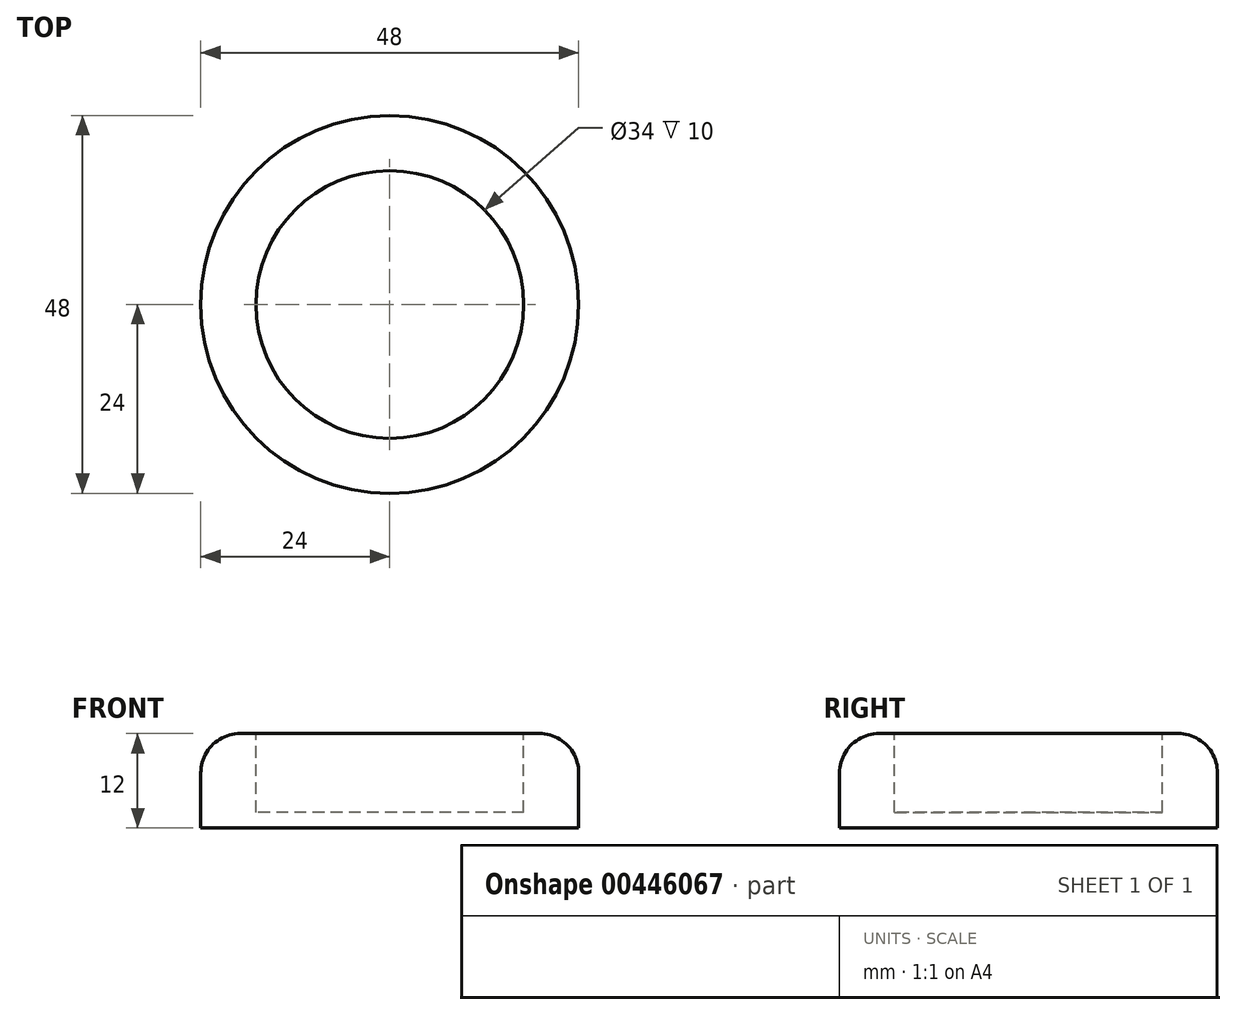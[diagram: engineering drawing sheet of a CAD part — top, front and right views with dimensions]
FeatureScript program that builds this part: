
annotation { "Feature Type Name" : "Feature", "Feature Type Description" : "" }
export const myFeature = defineFeature(function(context is Context, id is Id, definition is map)
    precondition{}
    {
        {
            var Q0;
            Q0=qCreatedBy(makeId("Top.planeOp"),FACE);
            var sketch = newSketch(context, id + "F0", { "sketchPlane" : qUnion([Q0])});
            skCircle(sketch, "E0", {"center": v(0, 0) * mm, "radius": 24 * mm});
            skSolve(sketch);
        }
        {
            var Q0;
            Q0=makeQuery(id+"F0.imprint","IMPRINT",FACE,{"disambiguationData":[TD([[makeQuery(id+"F0.imprint","IMPRINT",EDGE,{"derivedFrom":sQuery(id+"F0.wireOp",EDGE,"E0")}),1.0]])]});
            extrude(context, id + "F1", {"entities" : qUnion([Q0]), "depth" : 12 * mm});
        }
        {
            var Q0;
            Q0=makeQuery(id+"F1.opExtrude","CAP_EDGE",EDGE,{"disambiguationData":[OSD([sQuery(id+"F0.wireOp",EDGE,"E0")])],"isStart":false});
            fillet(context, id + "F2", {"entities" : qUnion([Q0]), "radius" : 5 * mm, "tangentPropagation" : true, "allowEdgeOverflow" : false});
        }
        {
            var Q0;
            Q0=makeQuery(id+"F1.opExtrude","CAP_FACE",FACE,{"disambiguationData":[OSD([sQuery(id+"F0.wireOp",EDGE,"E0")])],"isStart":false});
            var sketch = newSketch(context, id + "F3", { "sketchPlane" : qUnion([Q0])});
            skCircle(sketch, "E1", {"center": v(0, 0) * mm, "radius": 17 * mm});
            skSolve(sketch);
        }
        {
            var Q0;
            Q0=makeQuery(id+"F3.imprint","IMPRINT",FACE,{"disambiguationData":[TD([[makeQuery(id+"F3.imprint","IMPRINT",EDGE,{"derivedFrom":sQuery(id+"F3.wireOp",EDGE,"E1")}),1.0]])]});
            extrude(context, id + "F4", {"entities" : qUnion([Q0]), "operationType" : NewBodyOperationType.REMOVE, "oppositeDirection" : true, "depth" : 10 * mm});
        }
    });
